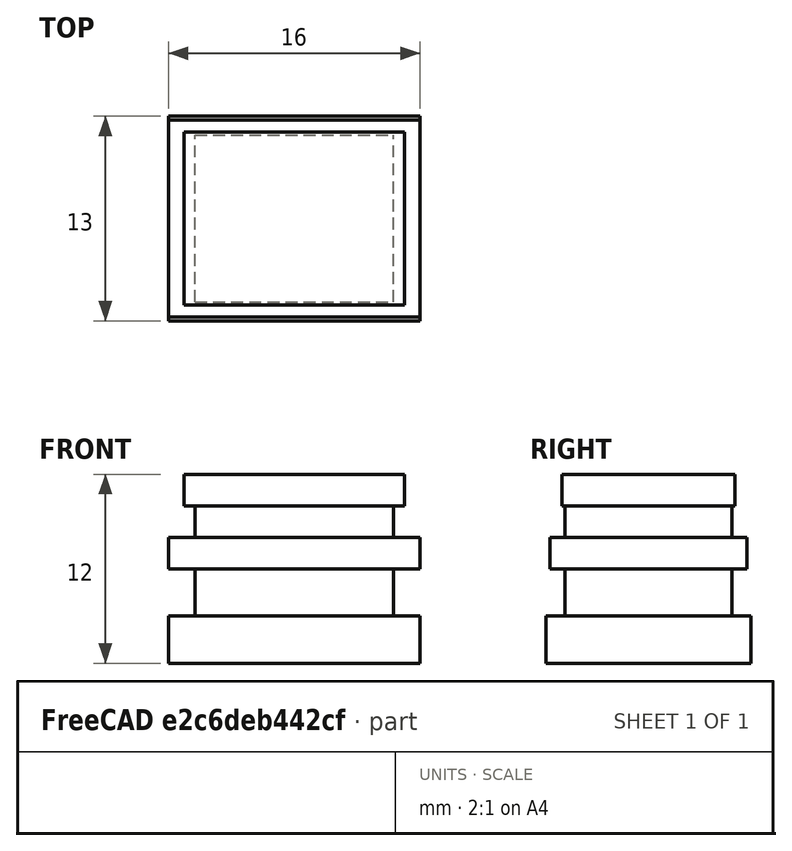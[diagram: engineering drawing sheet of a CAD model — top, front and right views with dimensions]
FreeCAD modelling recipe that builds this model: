
FCSTD DOCUMENT  (FreeCAD 0.19R0.19.2)
Label: 02
License: All rights reserved
LicenseURL: http://en.wikipedia.org/wiki/All_rights_reserved
objects: Part::Box×5, Sketcher::SketchObject×1
note: 6 computed .brp shape members not serialized (recipe doc carries the construction recipe); baked Part::Feature solids carry a one-line shape summary decoded from their .brp

FEATURE [Sketcher::SketchObject] Sketch
  FullyConstrained = true
FEATURE [Part::Box] Box  label="Cube"
  AttacherType = Attacher::AttachEngine3D
  Height = 3
  Length = 12.6
  Placement = pos=(1.7,1.2,3) rot=(0,0,1;0rad)
  Width = 10.6
FEATURE [Part::Box] Box001  label="Cube001"
  AttacherType = Attacher::AttachEngine3D
  Height = 3
  Length = 16
  Width = 13
FEATURE [Part::Box] Box002  label="Cube002"
  AttacherType = Attacher::AttachEngine3D
  Height = 2
  Length = 16
  Placement = pos=(0,0.25,6) rot=(0,0,1;0rad)
  Width = 12.5
FEATURE [Part::Box] Box003  label="Cube003"
  AttacherType = Attacher::AttachEngine3D
  Height = 2
  Length = 12.6
  Placement = pos=(1.7,1.2,8) rot=(0,0,1;0rad)
  Width = 10.6
FEATURE [Part::Box] Box004  label="Cube004"
  AttacherType = Attacher::AttachEngine3D
  Height = 2
  Length = 14
  Placement = pos=(1,1,10) rot=(0,0,1;0rad)
  Width = 11
